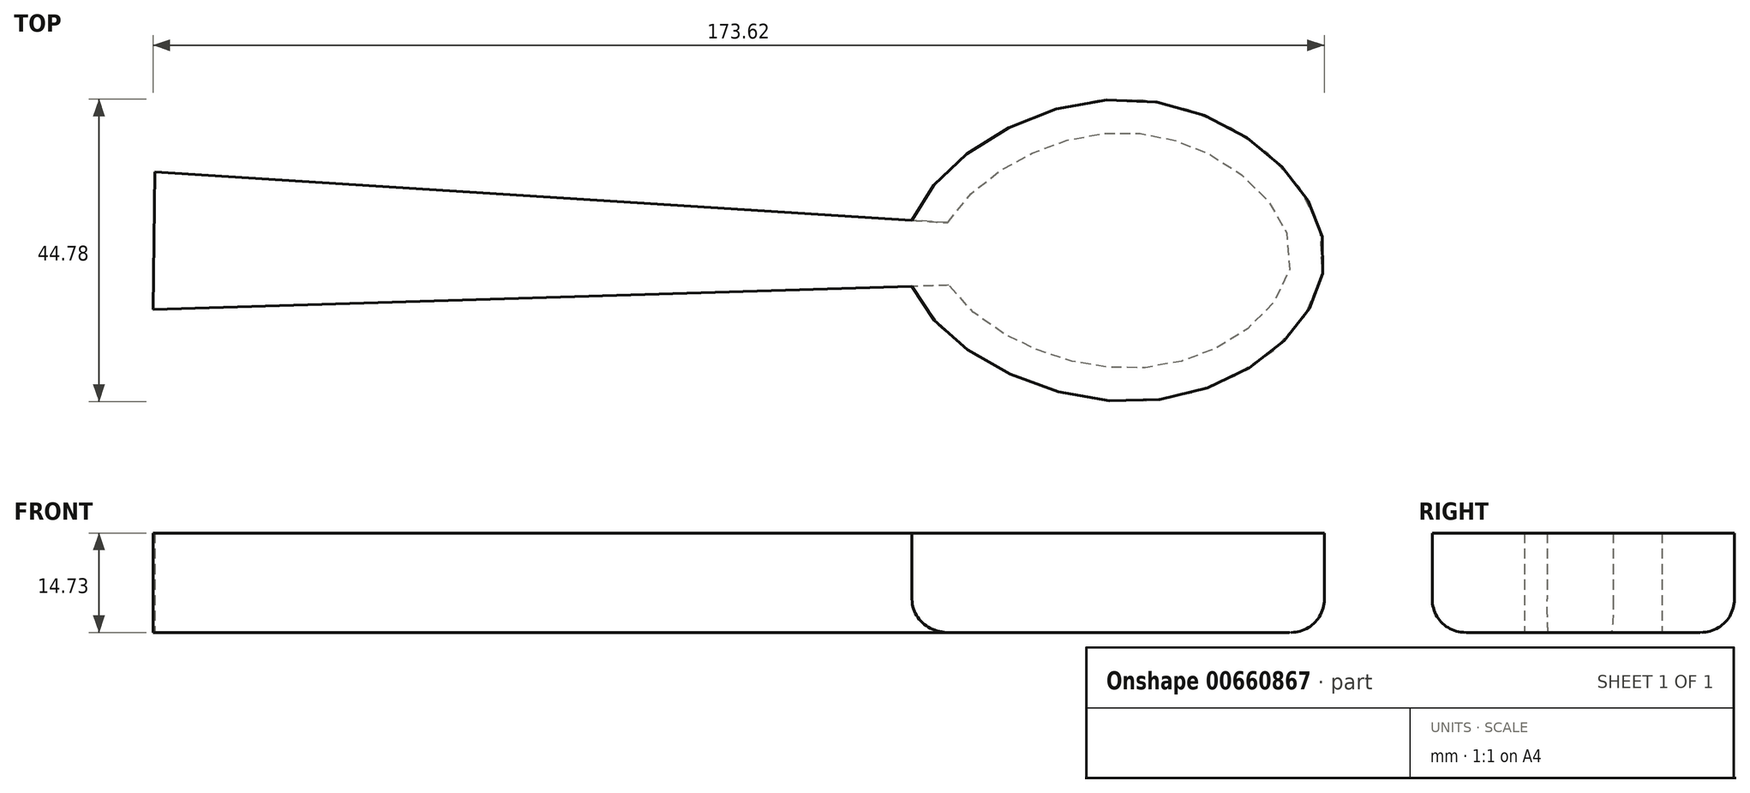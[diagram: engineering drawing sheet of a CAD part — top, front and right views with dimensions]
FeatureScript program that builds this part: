
annotation { "Feature Type Name" : "Feature", "Feature Type Description" : "" }
export const myFeature = defineFeature(function(context is Context, id is Id, definition is map)
    precondition{}
    {
        {
            var Q0;
            Q0=qCreatedBy(makeId("Top.planeOp"),FACE);
            var sketch = newSketch(context, id + "F0", { "sketchPlane" : qUnion([Q0])});
            skFitSpline(sketch, "E0", {"points": [v(0, 23.2) * mm, v(29.46, 0) * mm, v(1.61, -21.56) * mm, v(-32.69, 0) * mm, v(0, 23.2) * mm]});
            skLineSegment(sketch, "E1", {"start": v(-31.66, 5.26) * mm, "end": v(-143.88, 12.46) * mm});
            skLineSegment(sketch, "E2", {"start": v(-31.65, -4.53) * mm, "end": v(-144.16, -7.93) * mm});
            skLineSegment(sketch, "E3", {"start": v(-143.88, 12.46) * mm, "end": v(-144.16, -7.93) * mm});
            skLineSegment(sketch, "E4", {"start": v(-45.76, 6.17) * mm, "end": v(-45.43, -4.94) * mm});
            skSolve(sketch);
        }
        {
            var Q0;
            Q0 = qSketchRegion(id + "F0", true);
            extrude(context, id + "F1", {"entities" : qUnion([Q0]), "depth" : 14.73 * mm, "offsetDistance" : 25.4 * mm});
        }
        {
            var Q0;
            Q0=makeQuery(id+"F1.opExtrude","CAP_FACE",FACE,{"disambiguationData":[OSD([sQuery(id+"F0.wireOp",EDGE,"E0"),sQuery(id+"F0.wireOp",EDGE,"E1"),sQuery(id+"F0.wireOp",EDGE,"E2"),sQuery(id+"F0.wireOp",EDGE,"E3")])],"isStart":false});
            var sketch = newSketch(context, id + "F2", { "sketchPlane" : qUnion([Q0])});
            skSolve(sketch);
        }
        {
            var Q0;
            Q0=makeQuery(id+"F1.opExtrude","CAP_EDGE",EDGE,{"disambiguationData":[OSD([sQuery(id+"F0.wireOp",EDGE,"E0")])],"isStart":true});
            fillet(context, id + "F3", {"entities" : qUnion([Q0]), "radius" : 4.9 * mm, "tangentPropagation" : true, "allowEdgeOverflow" : false});
        }
    });
